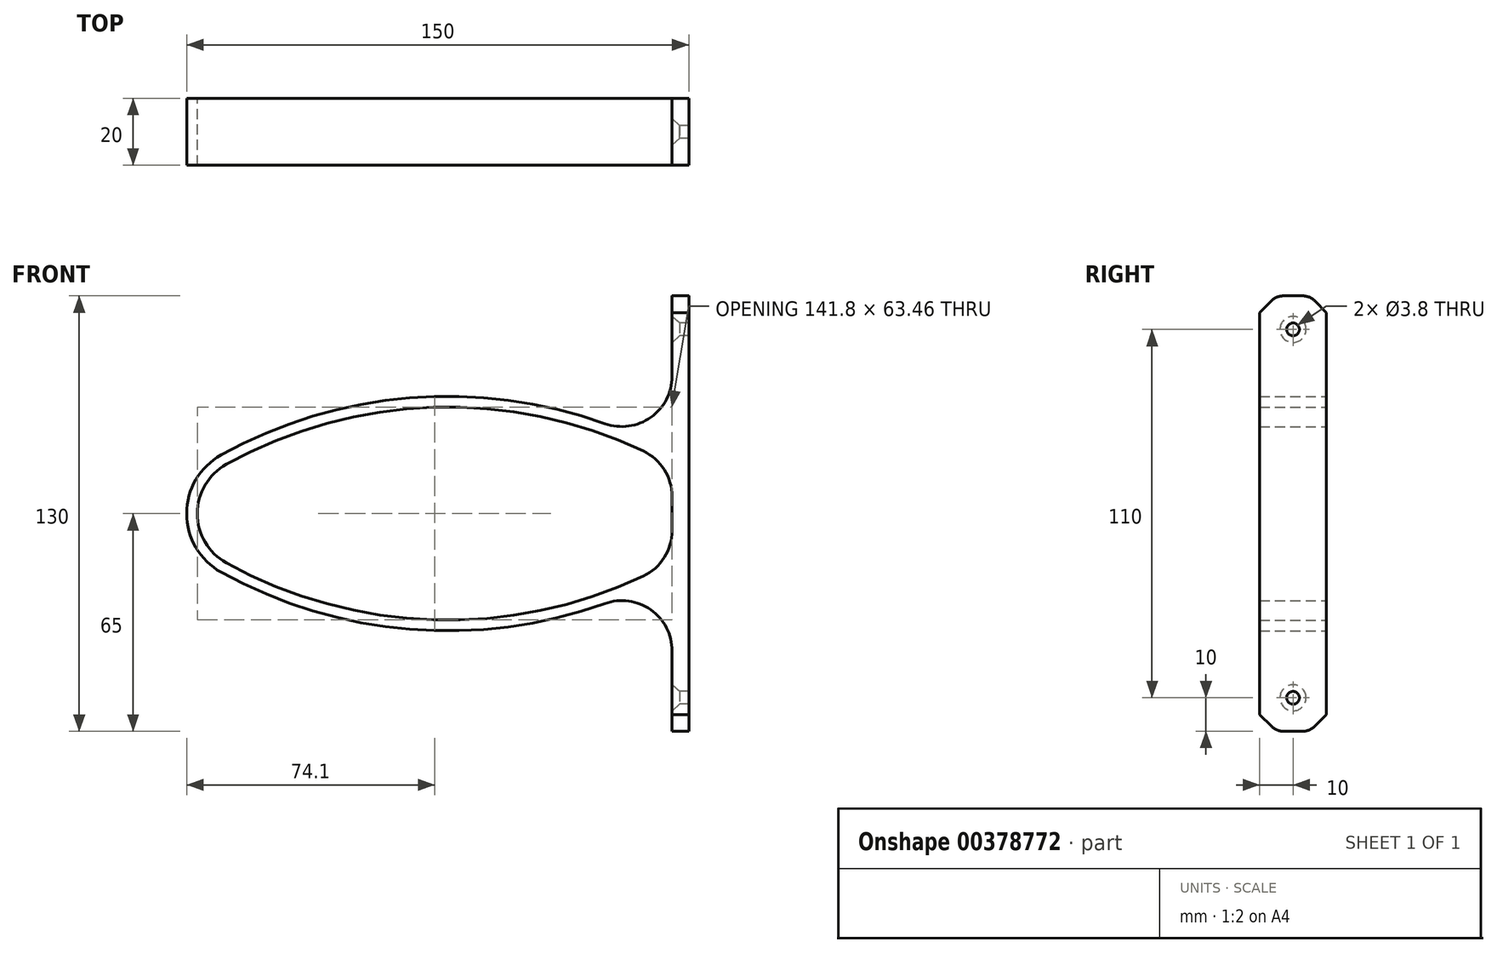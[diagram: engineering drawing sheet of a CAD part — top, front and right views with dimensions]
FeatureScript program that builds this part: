
annotation { "Feature Type Name" : "Feature", "Feature Type Description" : "" }
export const myFeature = defineFeature(function(context is Context, id is Id, definition is map)
    precondition{}
    {
        {
            var Q0;
            Q0=qCreatedBy(makeId("Front.planeOp"),FACE);
            var sketch = newSketch(context, id + "F0", { "sketchPlane" : qUnion([Q0])});
            skLineSegment(sketch, "E0.bottom", {"start": v(0, 65) * mm, "end": v(-5, 65) * mm});
            skLineSegment(sketch, "E0.top", {"start": v(0, -65) * mm, "end": v(-5, -65) * mm});
            skLineSegment(sketch, "E0.left", {"start": v(0, 65) * mm, "end": v(0, -65) * mm});
            skLineSegment(sketch, "E0.right", {"start": v(-5, 65) * mm, "end": v(-5, -65) * mm});
            skLineSegment(sketch, "E1", {"start": v(0, 0) * mm, "end": v(-150, 0) * mm, "construction": true});
            skArc(sketch, "E2", {"start": v(0, 15) * mm, "mid": v(-69.51, 34.98) * mm, "end": v(-139.7, 17.5) * mm});
            skArc(sketch, "E3", {"start": v(-139.7, 17.5) * mm, "mid": v(-147.23, 10.16) * mm, "end": v(-150, 0) * mm});
            skArc(sketch, "E4.MirrorCS", {"start": v(-139.7, -17.5) * mm, "mid": v(-147.23, -10.16) * mm, "end": v(-150, 0) * mm});
            skArc(sketch, "E5.MirrorCS", {"start": v(0, -15) * mm, "mid": v(-69.51, -34.98) * mm, "end": v(-139.7, -17.5) * mm});
            skArc(sketch, "E6.0", {"start": v(-5, 14.21) * mm, "mid": v(-71.5, 31.8) * mm, "end": v(-138.14, 14.7) * mm});
            skArc(sketch, "E6.1", {"start": v(-138.14, 14.7) * mm, "mid": v(-144.47, 8.53) * mm, "end": v(-146.8, 0) * mm});
            skArc(sketch, "E6.2", {"start": v(-138.14, -14.7) * mm, "mid": v(-144.47, -8.53) * mm, "end": v(-146.8, 0) * mm});
            skArc(sketch, "E6.3", {"start": v(-5, -14.21) * mm, "mid": v(-71.5, -31.8) * mm, "end": v(-138.14, -14.7) * mm});
            skPoint(sketch, "E7", {"position": v(-5, 55) * mm});
            skPoint(sketch, "E8", {"position": v(-5, -55) * mm});
            skSolve(sketch);
        }
        {
            var Q0;
            {var subQ3=sQuery(id+"F0.wireOp",EDGE,"E2");var subQ7=sQuery(id+"F0.wireOp",EDGE,"E0.left");var subQ8=makeQuery(id+"F0.imprint","INTERSECT",VERTEX,{"derivedFrom":[subQ7,subQ3]});Q0=makeQuery(id+"F0.imprint","IMPRINT",FACE,{"disambiguationData":[TD([[makeQuery(id+"F0.imprint","IMPRINT",EDGE,{"disambiguationData":[TD([[subQ8,-1.0]])],"derivedFrom":subQ7}),-1.0]])]});}
            var Q1;
            {var subQ0=sQuery(id+"F0.wireOp",EDGE,"E0.bottom");Q1=makeQuery(id+"F0.imprint","IMPRINT",FACE,{"disambiguationData":[TD([[makeQuery(id+"F0.imprint","IMPRINT",EDGE,{"derivedFrom":subQ0}),1.0]])]});}
            var Q2;
            {var subQ0=sQuery(id+"F0.wireOp",EDGE,"E0.top");Q2=makeQuery(id+"F0.imprint","IMPRINT",FACE,{"disambiguationData":[TD([[makeQuery(id+"F0.imprint","IMPRINT",EDGE,{"derivedFrom":subQ0}),-1.0]])]});}
            var Q3;
            {var subQ0=sQuery(id+"F0.wireOp",EDGE,"E3");Q3=makeQuery(id+"F0.imprint","IMPRINT",FACE,{"disambiguationData":[TD([[makeQuery(id+"F0.imprint","IMPRINT",EDGE,{"derivedFrom":subQ0}),1.0]])]});}
            extrude(context, id + "F1", {"entities" : qUnion([Q0, Q1, Q2, Q3]), "endBound" : BoundingType.SYMMETRIC, "depth" : 20 * mm});
        }
        {
            var Q0;
            {var subQ0=sQuery(id+"F0.wireOp",EDGE,"E0.right");Q0=makeQuery(id+"F1.opExtrude","SWEPT_FACE",FACE,{"disambiguationData":[OSD([subQ0]),TDD([makeQuery(id+"F0.imprint","IMPRINT",EDGE,{"disambiguationData":[TD([[makeQuery(id+"F0.imprint","INTERSECT",VERTEX,{"derivedFrom":[sQuery(id+"F0.wireOp",EDGE,"E0.bottom"),subQ0]}),-1.0]])],"derivedFrom":subQ0})])]});}
            var sketch = newSketch(context, id + "F2", { "sketchPlane" : qUnion([Q0])});
            skPoint(sketch, "E9.0", {"position": v(0, 55) * mm});
            skPoint(sketch, "E9.1", {"position": v(0, -55) * mm});
            skSolve(sketch);
        }
        {
            var Q0;
            Q0=sQuery(id+"F2.wireOp",VERTEX,"E9.0");
            var Q1;
            Q1=sQuery(id+"F2.wireOp",VERTEX,"E9.1");
            var Q2;
            Q2=makeQuery(id+"F1.opExtrude","SWEPT_BODY",BODY,{"disambiguationData":[OSD([sQuery(id+"F0.wireOp",EDGE,"E0.bottom"),sQuery(id+"F0.wireOp",EDGE,"E0.top"),sQuery(id+"F0.wireOp",EDGE,"E0.left"),sQuery(id+"F0.wireOp",EDGE,"E0.right"),sQuery(id+"F0.wireOp",EDGE,"E2"),sQuery(id+"F0.wireOp",EDGE,"E3"),sQuery(id+"F0.wireOp",EDGE,"E4.MirrorCS"),sQuery(id+"F0.wireOp",EDGE,"E5.MirrorCS"),sQuery(id+"F0.wireOp",EDGE,"E6.0"),sQuery(id+"F0.wireOp",EDGE,"E6.1"),sQuery(id+"F0.wireOp",EDGE,"E6.2"),sQuery(id+"F0.wireOp",EDGE,"E6.3")])]});
            hole(context, id + "F3", {"style" : HoleStyle.C_SINK, "endStyle" : HoleEndStyle.THROUGH, "standardTappedOrClearance" : lookupTablePath({ "standard" : "ANSI", "fit" : "Normal (ASME)", "size" : "#6", "type" : "Clearance" }), "standardBlindInLast" : lookupTablePath({ "fit" : "Free", "standard" : "ANSI", "size" : "#6", "type" : "Clearance" }), "holeDiameter" : 3.8 * mm, "cSinkDiameter" : 7.8 * mm, "cSinkAngle" : 82 * degree, "isTappedThrough" : true, "tappedDepth" : 12 * mm, "tapClearance" : 3, "locations" : qUnion([Q0, Q1]), "scope" : qUnion([Q2])});
        }
        {
            var Q0;
            Q0=makeQuery(id+"F1.opExtrude","CAP_EDGE",EDGE,{"disambiguationData":[OSD([sQuery(id+"F0.wireOp",EDGE,"E0.bottom")])],"isStart":false});
            var Q1;
            Q1=makeQuery(id+"F1.opExtrude","CAP_EDGE",EDGE,{"disambiguationData":[OSD([sQuery(id+"F0.wireOp",EDGE,"E0.bottom")])],"isStart":true});
            var Q2;
            Q2=makeQuery(id+"F1.opExtrude","CAP_EDGE",EDGE,{"disambiguationData":[OSD([sQuery(id+"F0.wireOp",EDGE,"E0.top")])],"isStart":false});
            var Q3;
            Q3=makeQuery(id+"F1.opExtrude","CAP_EDGE",EDGE,{"disambiguationData":[OSD([sQuery(id+"F0.wireOp",EDGE,"E0.top")])],"isStart":true});
            chamfer(context, id + "F4", {"entities" : qUnion([Q0, Q1, Q2, Q3]), "width" : 5 * mm, "tangentPropagation" : true});
        }
        {
            var Q0;
            {var subQ0=sQuery(id+"F0.wireOp",EDGE,"E0.top");Q0=makeQuery(id+"F4.opChamfer","BLEND_EDGE",EDGE,{"blendedFrom":[makeQuery(id+"F1.opExtrude","CAP_EDGE",EDGE,{"disambiguationData":[OSD([subQ0])],"isStart":false}),makeQuery(id+"F1.opExtrude","SWEPT_FACE",FACE,{"disambiguationData":[OSD([subQ0])]})],"blendedInto":[makeQuery(id+"F1.opExtrude","SWEPT_FACE",FACE,{"disambiguationData":[OSD([subQ0])]})]});}
            var Q1;
            {var subQ0=sQuery(id+"F0.wireOp",EDGE,"E0.top");Q1=makeQuery(id+"F4.opChamfer","BLEND_EDGE",EDGE,{"blendedFrom":[makeQuery(id+"F1.opExtrude","CAP_EDGE",EDGE,{"disambiguationData":[OSD([subQ0])],"isStart":true}),makeQuery(id+"F1.opExtrude","SWEPT_FACE",FACE,{"disambiguationData":[OSD([subQ0])]})],"blendedInto":[makeQuery(id+"F1.opExtrude","SWEPT_FACE",FACE,{"disambiguationData":[OSD([subQ0])]})]});}
            var Q2;
            {var subQ0=sQuery(id+"F0.wireOp",EDGE,"E0.bottom");Q2=makeQuery(id+"F4.opChamfer","BLEND_EDGE",EDGE,{"blendedFrom":[makeQuery(id+"F1.opExtrude","CAP_EDGE",EDGE,{"disambiguationData":[OSD([subQ0])],"isStart":false}),makeQuery(id+"F1.opExtrude","SWEPT_FACE",FACE,{"disambiguationData":[OSD([subQ0])]})],"blendedInto":[makeQuery(id+"F1.opExtrude","SWEPT_FACE",FACE,{"disambiguationData":[OSD([subQ0])]})]});}
            var Q3;
            {var subQ0=sQuery(id+"F0.wireOp",EDGE,"E0.bottom");Q3=makeQuery(id+"F4.opChamfer","BLEND_EDGE",EDGE,{"blendedFrom":[makeQuery(id+"F1.opExtrude","CAP_EDGE",EDGE,{"disambiguationData":[OSD([subQ0])],"isStart":true}),makeQuery(id+"F1.opExtrude","SWEPT_FACE",FACE,{"disambiguationData":[OSD([subQ0])]})],"blendedInto":[makeQuery(id+"F1.opExtrude","SWEPT_FACE",FACE,{"disambiguationData":[OSD([subQ0])]})]});}
            fillet(context, id + "F5", {"entities" : qUnion([Q0, Q1, Q2, Q3]), "radius" : 5 * mm, "tangentPropagation" : true, "allowEdgeOverflow" : false});
        }
        {
            var Q0;
            Q0=makeQuery(id+"F1.opExtrude","SWEPT_EDGE",EDGE,{"disambiguationData":[OSD([sQuery(id+"F0.wireOp",EDGE,"E0.right"),sQuery(id+"F0.wireOp",EDGE,"E6.0")])]});
            var Q1;
            Q1=makeQuery(id+"F1.opExtrude","SWEPT_EDGE",EDGE,{"disambiguationData":[OSD([sQuery(id+"F0.wireOp",EDGE,"E0.right"),sQuery(id+"F0.wireOp",EDGE,"E2")])]});
            var Q2;
            Q2=makeQuery(id+"F1.opExtrude","SWEPT_EDGE",EDGE,{"disambiguationData":[OSD([sQuery(id+"F0.wireOp",EDGE,"E0.right"),sQuery(id+"F0.wireOp",EDGE,"E5.MirrorCS")])]});
            var Q3;
            Q3=makeQuery(id+"F1.opExtrude","SWEPT_EDGE",EDGE,{"disambiguationData":[OSD([sQuery(id+"F0.wireOp",EDGE,"E0.right"),sQuery(id+"F0.wireOp",EDGE,"E6.3")])]});
            fillet(context, id + "F6", {"entities" : qUnion([Q0, Q1, Q2, Q3]), "radius" : 15 * mm, "tangentPropagation" : true, "allowEdgeOverflow" : false});
        }
    });
